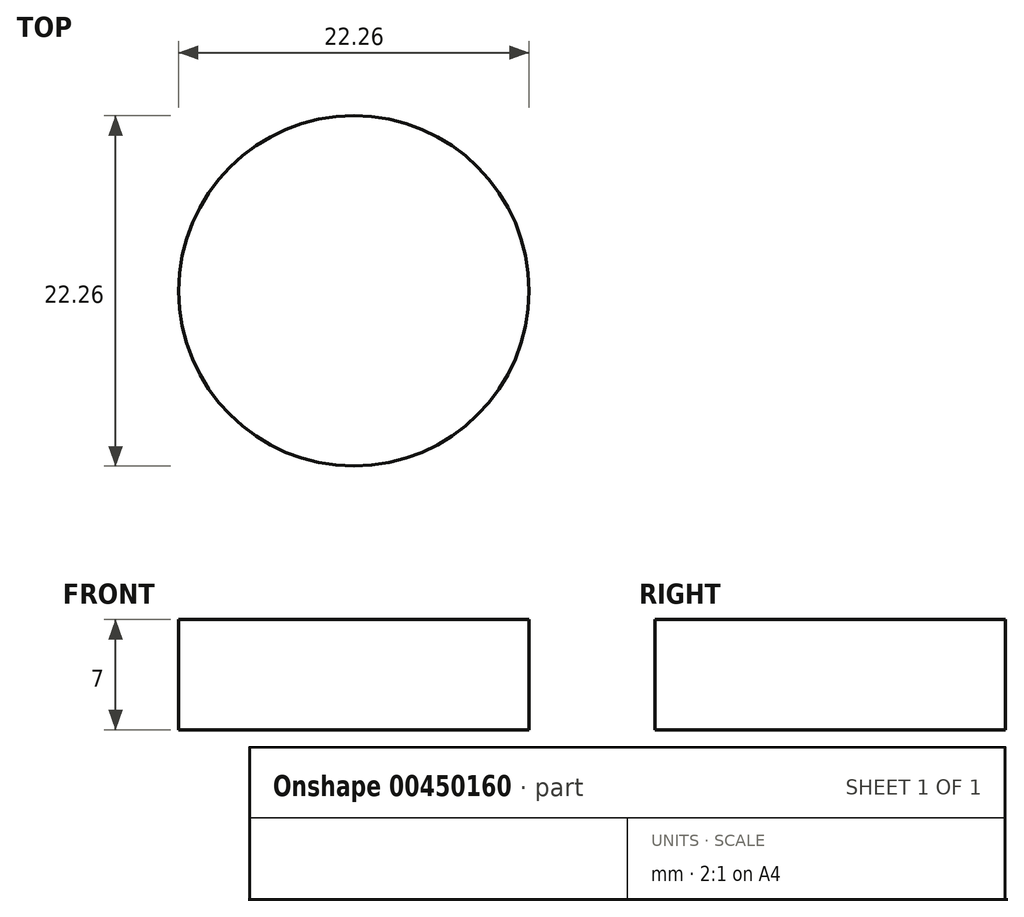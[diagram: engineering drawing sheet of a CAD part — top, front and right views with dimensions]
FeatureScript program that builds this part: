
annotation { "Feature Type Name" : "Feature", "Feature Type Description" : "" }
export const myFeature = defineFeature(function(context is Context, id is Id, definition is map)
    precondition{}
    {
        {
            var Q0;
            Q0=qCreatedBy(makeId("Top.planeOp"),FACE);
            var sketch = newSketch(context, id + "F0", { "sketchPlane" : qUnion([Q0])});
            skCircle(sketch, "E0", {"center": v(0, 0) * mm, "radius": 11.13 * mm});
            skSolve(sketch);
        }
        {
            var Q0;
            Q0 = qSketchRegion(id + "F0", true);
            extrude(context, id + "F1", {"entities" : qUnion([Q0]), "depth" : 7 * mm, "offsetDistance" : 25 * mm});
        }
    });
